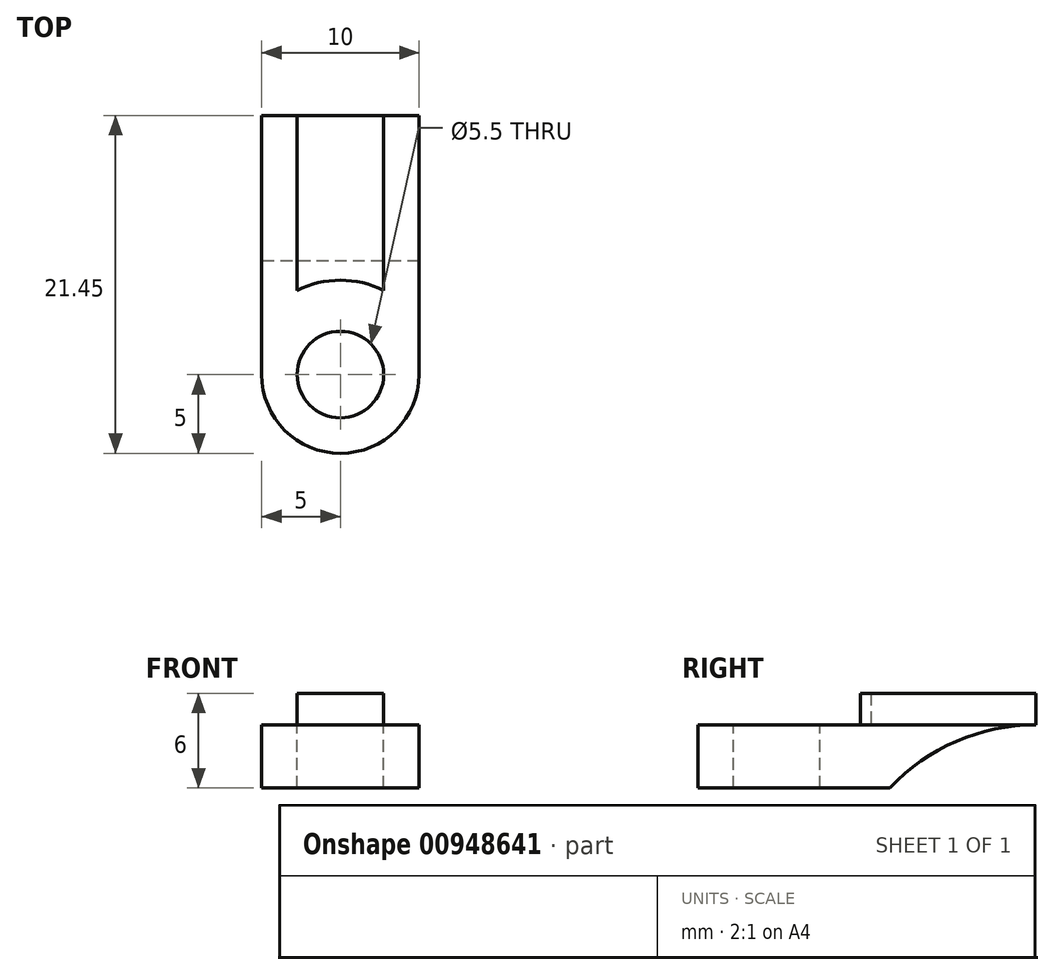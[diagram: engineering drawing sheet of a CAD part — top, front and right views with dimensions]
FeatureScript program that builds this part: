
annotation { "Feature Type Name" : "Feature", "Feature Type Description" : "" }
export const myFeature = defineFeature(function(context is Context, id is Id, definition is map)
    precondition{}
    {
        {
            var Q0;
            Q0=qCreatedBy(makeId("Right.planeOp"),FACE);
            var sketch = newSketch(context, id + "F0", { "sketchPlane" : qUnion([Q0])});
            skLineSegment(sketch, "E0", {"start": v(0, 0) * mm, "end": v(0, 25.38) * mm, "construction": true});
            skLineSegment(sketch, "E1", {"start": v(0, 0) * mm, "end": v(16.45, 0) * mm});
            skLineSegment(sketch, "E2", {"start": v(-5, -4) * mm, "end": v(7.2, -4) * mm});
            skLineSegment(sketch, "E3", {"start": v(16.45, 26.1) * mm, "end": v(16.45, -35.75) * mm, "construction": true});
            skArc(sketch, "E4", {"start": v(16.45, 0) * mm, "mid": v(11.41, -1.04) * mm, "end": v(7.2, -4) * mm});
            skLineSegment(sketch, "E5", {"start": v(-5, -4) * mm, "end": v(-5, 0) * mm});
            skLineSegment(sketch, "E6", {"start": v(-5, 0) * mm, "end": v(0, 0) * mm});
            skSolve(sketch);
        }
        {
            var Q0;
            Q0 = qSketchRegion(id + "F0", true);
            extrude(context, id + "F1", {"entities" : qUnion([Q0]), "endBound" : BoundingType.SYMMETRIC, "depth" : 10 * mm, "offsetDistance" : 25 * mm});
        }
        {
            var Q0;
            Q0=makeQuery(id+"F1.opExtrude","SWEPT_FACE",FACE,{"disambiguationData":[OSD([sQuery(id+"F0.wireOp",EDGE,"E1"),sQuery(id+"F0.wireOp",EDGE,"E6")])]});
            var sketch = newSketch(context, id + "F2", { "sketchPlane" : qUnion([Q0])});
            skCircle(sketch, "E7", {"center": v(0, 0) * mm, "radius": 2.75 * mm});
            skSolve(sketch);
        }
        {
            var Q0;
            Q0 = qSketchRegion(id + "F2", true);
            extrude(context, id + "F3", {"entities" : qUnion([Q0]), "operationType" : NewBodyOperationType.REMOVE, "endBound" : BoundingType.THROUGH_ALL, "oppositeDirection" : true, "depth" : 25 * mm, "offsetDistance" : 25 * mm});
        }
        {
            var Q0;
            Q0=makeQuery(id+"F1.opExtrude","CAP_EDGE",EDGE,{"disambiguationData":[OSD([sQuery(id+"F0.wireOp",EDGE,"E5")])],"isStart":false});
            var Q1;
            Q1=makeQuery(id+"F1.opExtrude","CAP_EDGE",EDGE,{"disambiguationData":[OSD([sQuery(id+"F0.wireOp",EDGE,"E5")])],"isStart":true});
            fillet(context, id + "F4", {"entities" : qUnion([Q0, Q1]), "radius" : 5 * mm, "tangentPropagation" : true, "allowEdgeOverflow" : false});
        }
        {
            var Q0;
            Q0=makeQuery(id+"F1.opExtrude","SWEPT_FACE",FACE,{"disambiguationData":[OSD([sQuery(id+"F0.wireOp",EDGE,"E1"),sQuery(id+"F0.wireOp",EDGE,"E6")])]});
            var sketch = newSketch(context, id + "F5", { "sketchPlane" : qUnion([Q0])});
            skLineSegment(sketch, "E8", {"start": v(-2.75, 5.33) * mm, "end": v(-2.75, 16.45) * mm});
            skLineSegment(sketch, "E9", {"start": v(2.75, 5.33) * mm, "end": v(2.75, 16.45) * mm});
            skLineSegment(sketch, "E10", {"start": v(2.75, 16.45) * mm, "end": v(-2.75, 16.45) * mm});
            skArc(sketch, "E11", {"start": v(2.75, 5.33) * mm, "mid": v(0, 6) * mm, "end": v(-2.75, 5.33) * mm});
            skPoint(sketch, "E12.orphan", {"position": v(2.75, 0) * mm});
            skPoint(sketch, "E13.orphan", {"position": v(-2.75, 0) * mm});
            skSolve(sketch);
        }
        {
            var Q0;
            Q0 = qSketchRegion(id + "F5", true);
            extrude(context, id + "F6", {"entities" : qUnion([Q0]), "operationType" : NewBodyOperationType.ADD, "depth" : 2 * mm, "offsetDistance" : 25 * mm});
        }
    });
